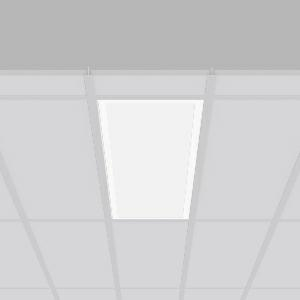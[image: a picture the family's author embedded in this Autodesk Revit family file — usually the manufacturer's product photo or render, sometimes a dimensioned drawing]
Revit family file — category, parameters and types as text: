
# Revit family: sidelite_eco_672378_002_1_04_4def
name_source: partatom
category: Lighting Fixtures
units: mm (PartAtom-declared; Revit-internal decimal feet)

## family parameters
Cut with Voids When Loaded = No
Host = Face
Light Source = No
Part Type = Normal
Room Calculation Point = No
Round Connector Dimension = Use Diameter
Shared = No

## types (1)
- SIDELITE ECO (1 x LED Modul 840, 3500 lm, 4000)
    Apparent Load = 29 VA
    CIE Flux Codes = 47 79 96 100 100
    Color Rendering = 80
    Color Temperature = 4000
    Default Elevation = 1800 mm
    Description = Series: SIDELITE ECO
Highly economical recessed luminaire with progressive LED technology. For escape route illumination. Frame made of aluminium, powder-coated. Diffuser: plastic, opal. Lightguide and diffuser made of non-yellowing plastic (PMMA). Lateral light emission (RZB SIDELITE technology) for homogeneous light distribution. External driver. Self-contained system with automatic self-test and feedback to the RZB monitoring system MULTIDIGIT. External driver with simple plug-in locking system. Extended connection cable (1.90 m). 
Colour: white
Length: 1245 mm
Width: 308 mm
Cut-out length: 1220 mm
Cut-out width: 285 mm
Recess height: 160 mm
Luminaire: recess height: 40 mm
Weight: 4.7 kg
Operating mode: maintained power mode
Duration time: 8 h
Lamp: LED
Socket: without socket
Colour temperature: 4000K
Colour rendering index (CRI): 80
System power: 29 W
Rated luminous flux: 3500 lm
Luminous flux, emergency: 240 lm
System power, emergency: -
Control gear: Regulated power supply
Protection class: I
Type of protection: IP 40
    Height = 0 mm  [stored 0 ft]
    Lamp = 1 x LED Modul 840
    Lamp Light Flux = 3500 lm
    Lamp count = 1
    Length = 1245 mm
    Lifetime = 50000 h
    Luminous efficacy = 121 lm/W
    Manufacturer = RZB
    ModVariant = No
    Model = 672378.002.1.04
    Mounting Place = Ceiling
    Mounting Type = Recessed
    Number of Poles = 1
    OnlyDefault = Yes
    Power Factor = 1
    Product Name = SIDELITE ECO
    Product group = Recessed modular luminaires
    ProductGroupID = 406
    Protection Class = Protection class I
    Protection Degree = IP 40
    RLX_Detail_Level = 1
    RLX_Emergency_Light_Flux = 240 lm
    RLX_Emergency_Type = 3
    RLX_Emergency_Type_DB = Yes
    RlxData = <blob elided: 30053 chars, md5=e03dd7b6>
    Socket = socket
    Standby Power = 0 W
    System Light Flux = 3500 lm
    System Power = 29 W
    Type Comments = Product without accessories
    Type Image = 312367.002.jpg
    URL = http://relux.com
    VarID = ---
    Voltage = 230 V
    Voltage Range = 220-240 V
    Weight = 0.00 kg
    Width = 308 mm

note: [stored X ft] marks values corroborated as IEEE doubles in the binary element streams (Revit-internal decimal feet)

## geometry (parser evidence)
native form markers: Blend x4, Sweep x11
no freeform markers — native parametric forms only
